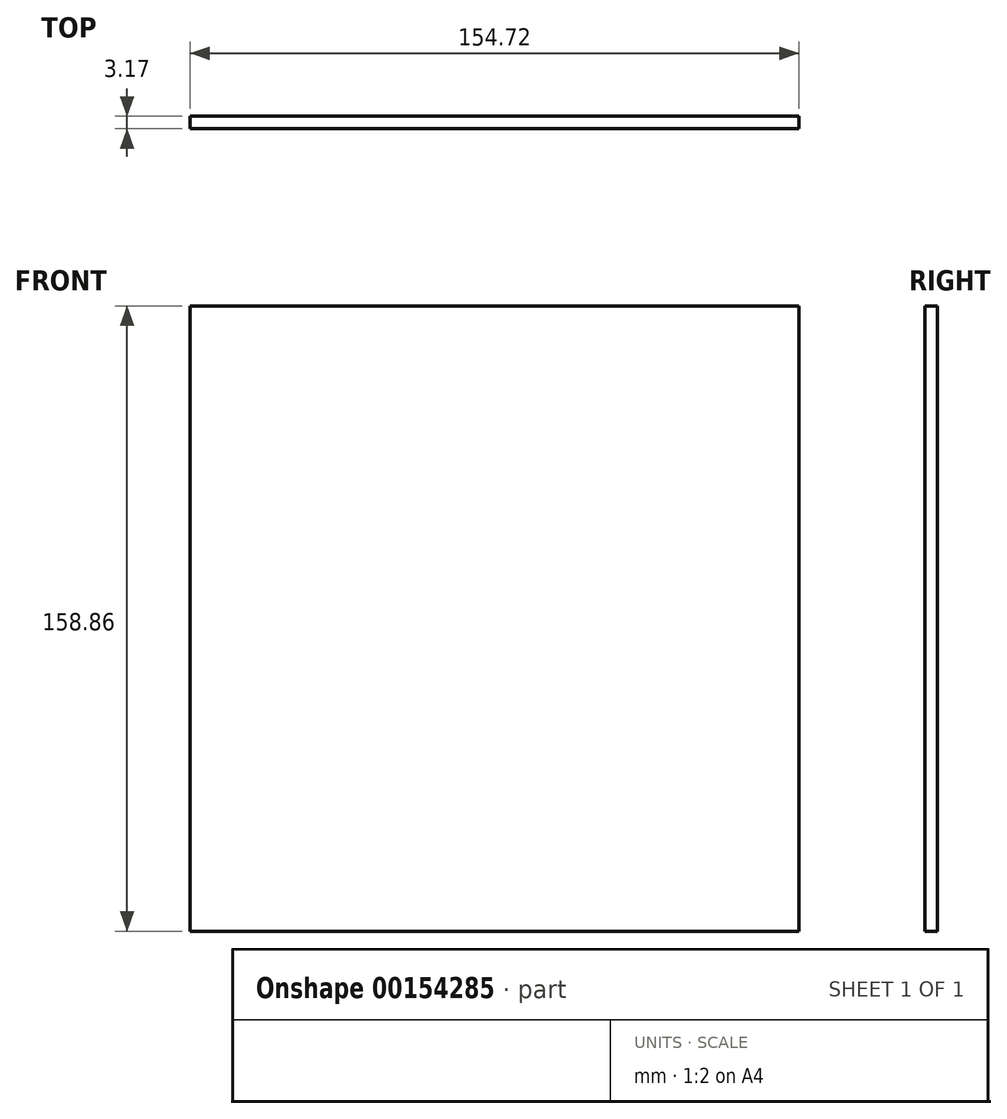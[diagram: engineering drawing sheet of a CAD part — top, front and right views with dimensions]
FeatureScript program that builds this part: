
annotation { "Feature Type Name" : "Feature", "Feature Type Description" : "" }
export const myFeature = defineFeature(function(context is Context, id is Id, definition is map)
    precondition{}
    {
        {
            var Q0;
            Q0=qCreatedBy(makeId("Front.planeOp"),FACE);
            var sketch = newSketch(context, id + "F0", { "sketchPlane" : qUnion([Q0])});
            skLineSegment(sketch, "E0.bottom", {"start": v(0, 0) * mm, "end": v(0, 0) * mm});
            skLineSegment(sketch, "E0.top", {"start": v(0, 0) * mm, "end": v(0, 0) * mm});
            skLineSegment(sketch, "E0.left", {"start": v(0, 0) * mm, "end": v(0, 0) * mm});
            skLineSegment(sketch, "E0.right", {"start": v(0, 0) * mm, "end": v(0, 0) * mm});
            skPoint(sketch, "E0.middle", {"position": v(0, 0) * mm});
            skLineSegment(sketch, "E1.bottom", {"start": v(77.36, 79.43) * mm, "end": v(-77.36, 79.43) * mm});
            skLineSegment(sketch, "E1.top", {"start": v(77.36, -79.43) * mm, "end": v(-77.36, -79.43) * mm});
            skLineSegment(sketch, "E1.left", {"start": v(77.36, 79.43) * mm, "end": v(77.36, -79.43) * mm});
            skLineSegment(sketch, "E1.right", {"start": v(-77.36, 79.43) * mm, "end": v(-77.36, -79.43) * mm});
            skSolve(sketch);
        }
        {
            var Q0;
            Q0=makeQuery(id+"F0.imprint","IMPRINT",FACE,{"disambiguationData":[TD([[makeQuery(id+"F0.imprint","IMPRINT",EDGE,{"derivedFrom":sQuery(id+"F0.wireOp",EDGE,"E1.bottom")}),1.0]])]});
            var sketch = newSketch(context, id + "F1", { "sketchPlane" : qUnion([Q0])});
            skLineSegment(sketch, "E2.bottom", {"start": v(59.74, 60.72) * mm, "end": v(-59.74, 60.72) * mm});
            skLineSegment(sketch, "E2.top", {"start": v(59.74, -60.72) * mm, "end": v(-59.74, -60.72) * mm});
            skLineSegment(sketch, "E2.left", {"start": v(59.74, 60.72) * mm, "end": v(59.74, -60.72) * mm});
            skLineSegment(sketch, "E2.right", {"start": v(-59.74, 60.72) * mm, "end": v(-59.74, -60.72) * mm});
            skPoint(sketch, "E2.middle", {"position": v(0, 0) * mm});
            skSolve(sketch);
        }
        {
            var Q0;
            Q0=makeQuery(id+"F1.imprint","IMPRINT",FACE,{"disambiguationData":[TD([[makeQuery(id+"F1.imprint","IMPRINT",EDGE,{"derivedFrom":sQuery(id+"F1.wireOp",EDGE,"E2.bottom")}),1.0]])]});
            var Q1;
            Q1=makeQuery(id+"F1.imprint","IMPRINT",FACE,{"disambiguationData":[TD([[makeQuery(id+"F1.imprint","IMPRINT",EDGE,{"derivedFrom":sQuery(id+"F1.wireOp",EDGE,"E2.bottom")}),-1.0]])]});
            extrude(context, id + "F2", {"entities" : qUnion([Q0, Q1]), "depth" : 3.17 * mm});
        }
    });
